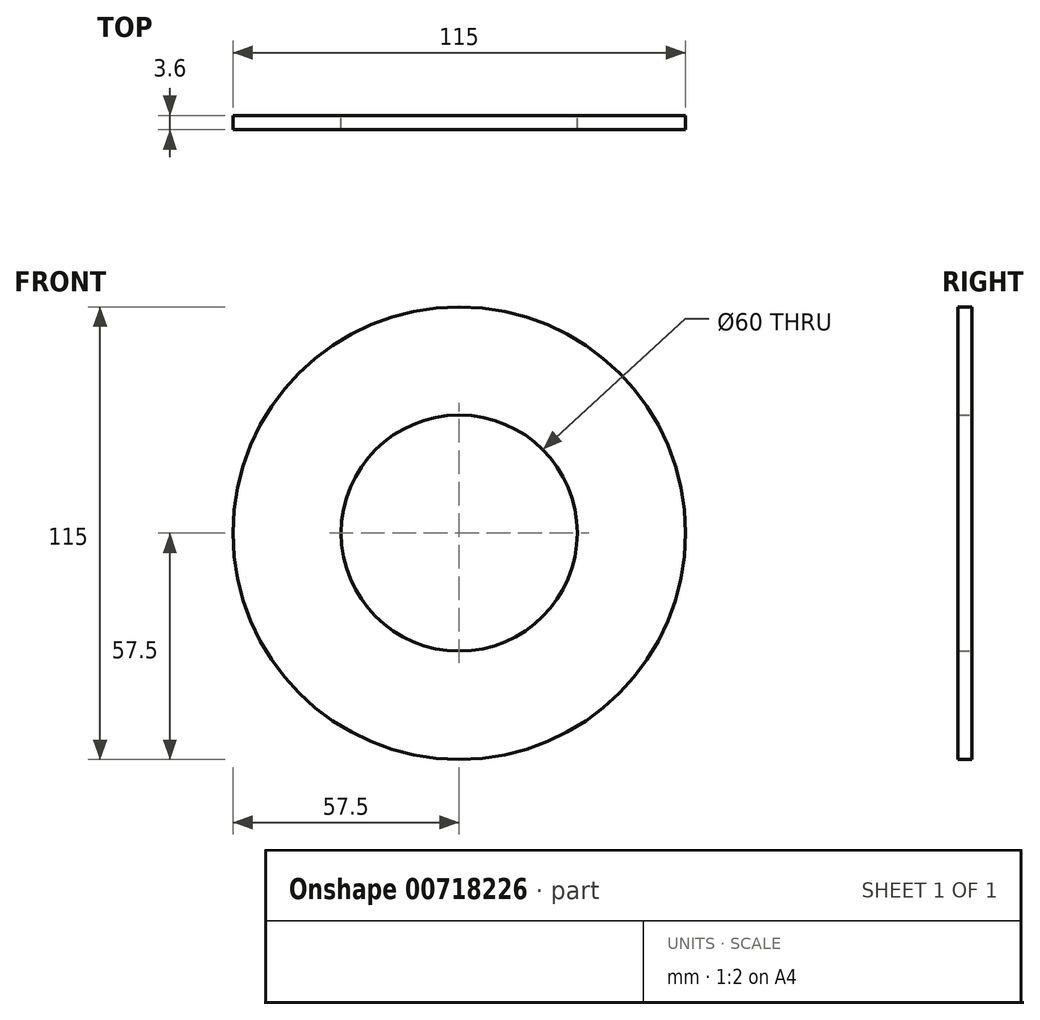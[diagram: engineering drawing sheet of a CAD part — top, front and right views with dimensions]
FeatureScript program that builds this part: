
annotation { "Feature Type Name" : "Feature", "Feature Type Description" : "" }
export const myFeature = defineFeature(function(context is Context, id is Id, definition is map)
    precondition{}
    {
        {
            var Q0;
            Q0=qCreatedBy(makeId("Front.planeOp"),FACE);
            var sketch = newSketch(context, id + "F0", { "sketchPlane" : qUnion([Q0])});
            skCircle(sketch, "E0", {"center": v(0, 0) * mm, "radius": 57.5 * mm});
            skCircle(sketch, "E1", {"center": v(0, 0) * mm, "radius": 30 * mm});
            skSolve(sketch);
        }
        {
            var Q0;
            Q0 = qSketchRegion(id + "F0", true);
            extrude(context, id + "F1", {"entities" : qUnion([Q0]), "depth" : 3.6 * mm, "offsetDistance" : 25 * mm});
        }
    });
